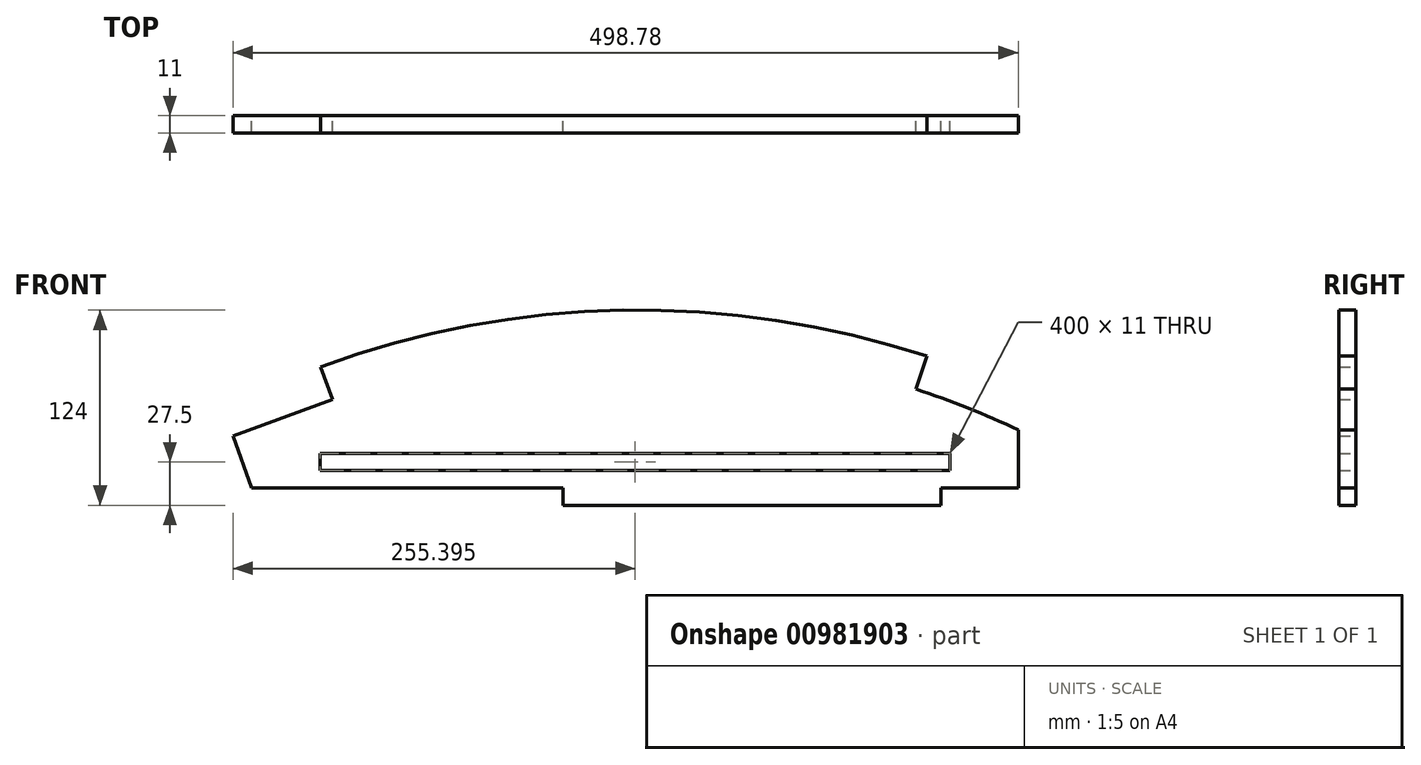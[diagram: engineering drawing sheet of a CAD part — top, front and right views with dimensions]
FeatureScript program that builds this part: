
annotation { "Feature Type Name" : "Feature", "Feature Type Description" : "" }
export const myFeature = defineFeature(function(context is Context, id is Id, definition is map)
    precondition{}
    {
        {
            var Q0;
            Q0=qCreatedBy(makeId("Front.planeOp"),FACE);
            var sketch = newSketch(context, id + "F0", { "sketchPlane" : qUnion([Q0])});
            skLineSegment(sketch, "E0", {"start": v(-249.39, -18) * mm, "end": v(-237.38, -51) * mm});
            skLineSegment(sketch, "E1", {"start": v(-237.38, -51) * mm, "end": v(-39.8, -51) * mm});
            skLineSegment(sketch, "E2", {"start": v(200.2, -51) * mm, "end": v(249.39, -51) * mm});
            skLineSegment(sketch, "E3", {"start": v(249.39, -51) * mm, "end": v(249.39, -14.19) * mm});
            skArc(sketch, "E4", {"start": v(249.39, -14.19) * mm, "mid": v(217.3, -0.19) * mm, "end": v(184.39, 11.8) * mm});
            skLineSegment(sketch, "E5", {"start": v(-249.39, -18) * mm, "end": v(-186.02, 5.33) * mm});
            skLineSegment(sketch, "E6", {"start": v(-194, -29) * mm, "end": v(206, -29) * mm});
            skLineSegment(sketch, "E7", {"start": v(-194, -40) * mm, "end": v(206, -40) * mm});
            skLineSegment(sketch, "E8", {"start": v(-194, -40) * mm, "end": v(-194, -29) * mm});
            skLineSegment(sketch, "E9", {"start": v(206, -40) * mm, "end": v(206, -29) * mm});
            skLineSegment(sketch, "E10", {"start": v(200.2, -51) * mm, "end": v(200.2, -62) * mm});
            skLineSegment(sketch, "E11", {"start": v(-39.8, -51) * mm, "end": v(-39.8, -62) * mm});
            skLineSegment(sketch, "E12", {"start": v(-39.8, -62) * mm, "end": v(200.2, -62) * mm});
            skArc(sketch, "E13", {"start": v(191.27, 32.69) * mm, "mid": v(-1.74, 61.91) * mm, "end": v(-193.62, 25.98) * mm});
            skLineSegment(sketch, "E14", {"start": v(-193.81, 25.9) * mm, "end": v(-193.62, 25.98) * mm});
            skLineSegment(sketch, "E15", {"start": v(-186.21, 5.26) * mm, "end": v(-193.81, 25.9) * mm});
            skLineSegment(sketch, "E16", {"start": v(184.39, 11.8) * mm, "end": v(191.27, 32.69) * mm});
            skSolve(sketch);
        }
        {
            var Q0;
            {var subQ1=sQuery(id+"F0.wireOp",EDGE,"E0");Q0=makeQuery(id+"F0.imprint","IMPRINT",FACE,{"disambiguationData":[TD([[makeQuery(id+"F0.imprint","IMPRINT",EDGE,{"derivedFrom":subQ1}),1.0]])]});}
            extrude(context, id + "F1", {"entities" : qUnion([Q0]), "depth" : 11 * mm, "offsetDistance" : 25 * mm});
        }
    });
